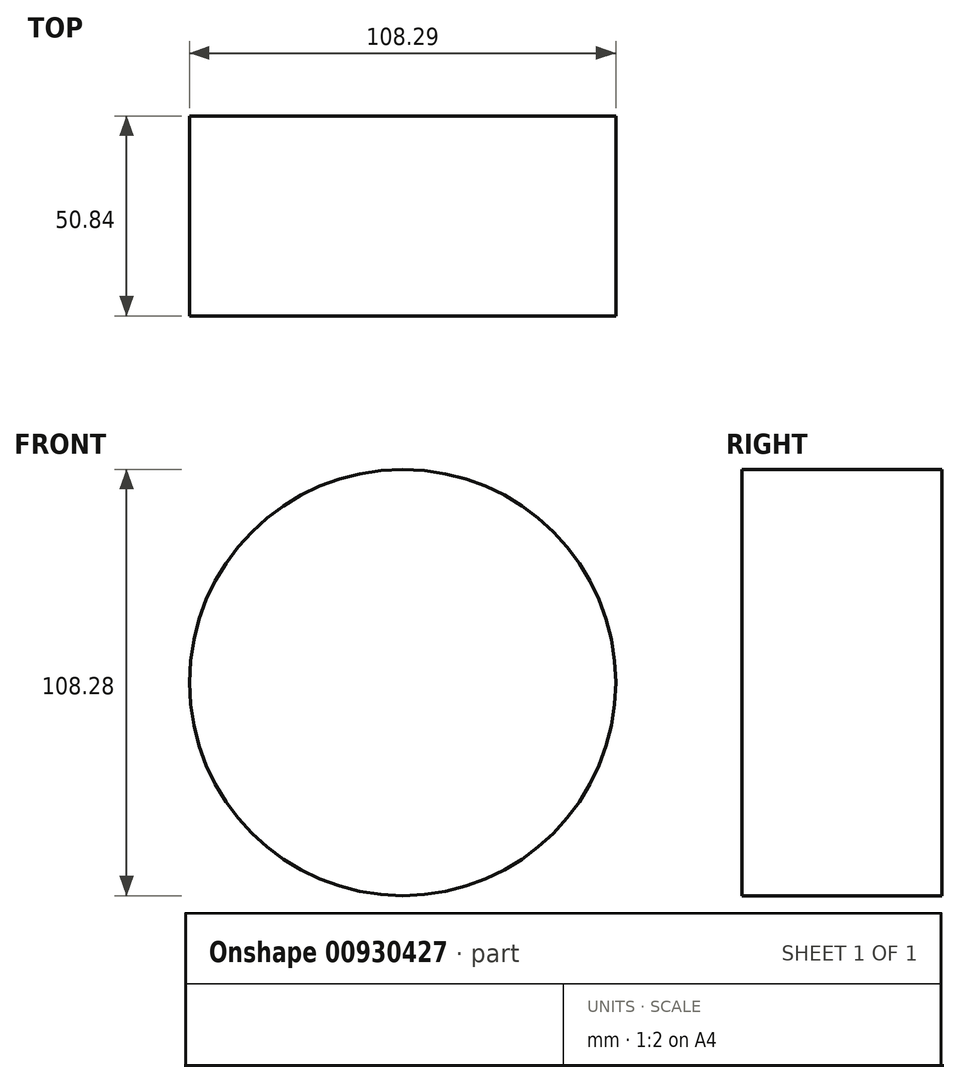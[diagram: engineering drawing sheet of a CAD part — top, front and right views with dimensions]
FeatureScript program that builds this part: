
annotation { "Feature Type Name" : "Feature", "Feature Type Description" : "" }
export const myFeature = defineFeature(function(context is Context, id is Id, definition is map)
    precondition{}
    {
        {
            var Q0;
            Q0=qCreatedBy(makeId("Top.planeOp"),FACE);
            var sketch = newSketch(context, id + "F0", { "sketchPlane" : qUnion([Q0])});
            skLineSegment(sketch, "E0.bottom", {"start": v(-35.94, 25.42) * mm, "end": v(18.2, 25.42) * mm});
            skLineSegment(sketch, "E0.top", {"start": v(-35.94, -25.42) * mm, "end": v(18.2, -25.42) * mm});
            skLineSegment(sketch, "E0.left", {"start": v(-35.94, 25.42) * mm, "end": v(-35.94, -25.42) * mm});
            skLineSegment(sketch, "E0.right", {"start": v(18.2, 25.42) * mm, "end": v(18.2, -25.42) * mm});
            skPoint(sketch, "E0.middle", {"position": v(-8.87, 0) * mm});
            skSolve(sketch);
        }
        {
            var Q0;
            Q0=makeQuery(id+"F0.imprint","IMPRINT",FACE,{"disambiguationData":[TD([[makeQuery(id+"F0.imprint","IMPRINT",EDGE,{"derivedFrom":sQuery(id+"F0.wireOp",EDGE,"E0.bottom")}),-1.0]])]});
            var Q1;
            Q1=sQuery(id+"F0.wireOp",EDGE,"E0.left");
            revolve(context, id + "F1", {"surfaceOperationType" : NewSurfaceOperationType.NEW, "entities" : qUnion([Q0]), "axis" : qUnion([Q1]), "revolveType" : RevolveType.FULL});
        }
    });
